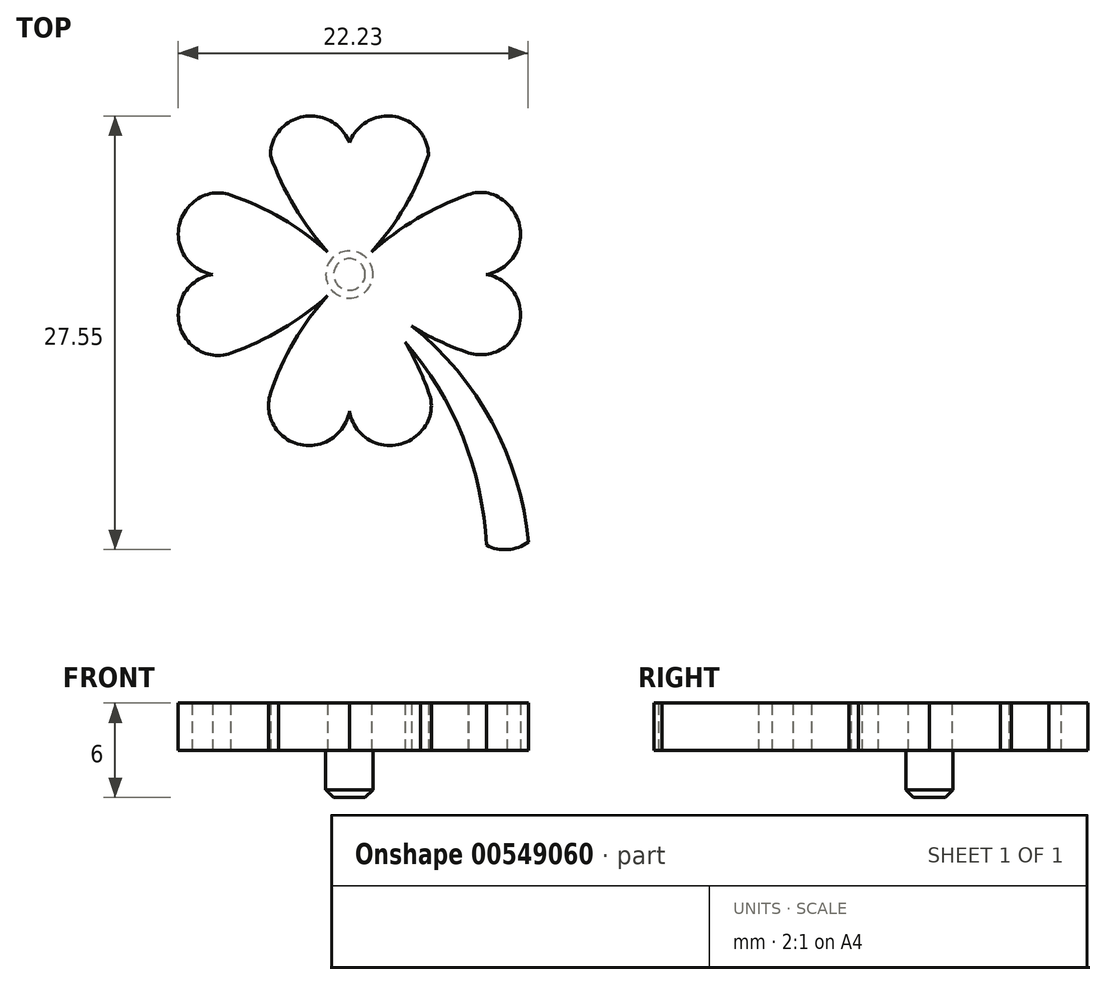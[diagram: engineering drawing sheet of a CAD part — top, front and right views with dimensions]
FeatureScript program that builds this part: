
annotation { "Feature Type Name" : "Feature", "Feature Type Description" : "" }
export const myFeature = defineFeature(function(context is Context, id is Id, definition is map)
    precondition{}
    {
        {
            var Q0;
            Q0=qCreatedBy(makeId("Top.planeOp"),FACE);
            var sketch = newSketch(context, id + "F0", { "sketchPlane" : qUnion([Q0])});
            skArc(sketch, "E0", {"start": v(-4.5, 9.05) * mm, "mid": v(-4.89, 8.35) * mm, "end": v(-5.02, 7.55) * mm});
            skArc(sketch, "E1", {"start": v(0, 8.36) * mm, "mid": v(-2.05, 10.04) * mm, "end": v(-4.5, 9.05) * mm});
            skLineSegment(sketch, "E2", {"start": v(0, 8.36) * mm, "end": v(0, 1.22) * mm, "construction": true});
            skLineSegment(sketch, "E3", {"start": v(0, 0) * mm, "end": v(0, 1.22) * mm, "construction": true});
            skArc(sketch, "E4.MirrorCS", {"start": v(4.5, 9.05) * mm, "mid": v(4.88, 8.36) * mm, "end": v(5.02, 7.6) * mm});
            skArc(sketch, "E5.MirrorCS", {"start": v(0, 8.36) * mm, "mid": v(2.05, 10.04) * mm, "end": v(4.5, 9.05) * mm});
            skArc(sketch, "E6.1.0", {"start": v(-10, 4.5) * mm, "mid": v(-8.85, 5.13) * mm, "end": v(-7.55, 5.05) * mm});
            skArc(sketch, "E6.1.1", {"start": v(-8.68, 0) * mm, "mid": v(-10.76, -1.84) * mm, "end": v(-10, -4.5) * mm});
            skLineSegment(sketch, "E6.1.2", {"start": v(-8.68, 0) * mm, "end": v(-1.22, 0) * mm, "construction": true});
            skArc(sketch, "E6.1.3", {"start": v(-10, -4.5) * mm, "mid": v(-8.82, -5.1) * mm, "end": v(-7.51, -5) * mm});
            skArc(sketch, "E6.1.4", {"start": v(-8.68, 0) * mm, "mid": v(-10.76, 1.84) * mm, "end": v(-10, 4.5) * mm});
            skArc(sketch, "E6.1.7", {"start": v(-8.68, 0) * mm, "mid": v(-10.76, -1.84) * mm, "end": v(-10, -4.5) * mm});
            skArc(sketch, "E6.1.8", {"start": v(-10, 4.5) * mm, "mid": v(-8.85, 5.13) * mm, "end": v(-7.55, 5.05) * mm});
            skArc(sketch, "E6.1.10", {"start": v(-8.68, 0) * mm, "mid": v(-10.76, 1.84) * mm, "end": v(-10, 4.5) * mm});
            skArc(sketch, "E6.1.11", {"start": v(-10, -4.5) * mm, "mid": v(-8.82, -5.1) * mm, "end": v(-7.51, -5) * mm});
            skArc(sketch, "E6.2.0", {"start": v(-4.5, -10) * mm, "mid": v(-5.09, -8.83) * mm, "end": v(-5, -7.53) * mm});
            skArc(sketch, "E6.2.1", {"start": v(0, -8.68) * mm, "mid": v(1.84, -10.76) * mm, "end": v(4.5, -10) * mm});
            skLineSegment(sketch, "E6.2.2", {"start": v(0, -8.68) * mm, "end": v(0, -1.22) * mm, "construction": true});
            skArc(sketch, "E6.2.3", {"start": v(4.5, -10) * mm, "mid": v(5.15, -8.82) * mm, "end": v(5.04, -7.49) * mm});
            skArc(sketch, "E6.2.4", {"start": v(0, -8.68) * mm, "mid": v(-1.84, -10.76) * mm, "end": v(-4.5, -10) * mm});
            skArc(sketch, "E6.2.7", {"start": v(0, -8.68) * mm, "mid": v(1.84, -10.76) * mm, "end": v(4.5, -10) * mm});
            skArc(sketch, "E6.2.8", {"start": v(-4.5, -10) * mm, "mid": v(-5.1, -8.83) * mm, "end": v(-5, -7.53) * mm});
            skArc(sketch, "E6.2.10", {"start": v(0, -8.68) * mm, "mid": v(-1.84, -10.76) * mm, "end": v(-4.5, -10) * mm});
            skArc(sketch, "E6.2.11", {"start": v(4.5, -10) * mm, "mid": v(5.15, -8.82) * mm, "end": v(5.04, -7.49) * mm});
            skArc(sketch, "E6.3.0", {"start": v(10, -4.5) * mm, "mid": v(8.84, -5.05) * mm, "end": v(7.57, -4.98) * mm});
            skArc(sketch, "E6.3.1", {"start": v(8.68, 0) * mm, "mid": v(10.76, 1.84) * mm, "end": v(10, 4.5) * mm});
            skLineSegment(sketch, "E6.3.2", {"start": v(8.68, 0) * mm, "end": v(1.22, 0) * mm, "construction": true});
            skArc(sketch, "E6.3.3", {"start": v(10, 4.5) * mm, "mid": v(8.85, 5.16) * mm, "end": v(7.53, 5.06) * mm});
            skArc(sketch, "E6.3.4", {"start": v(8.68, 0) * mm, "mid": v(10.76, -1.84) * mm, "end": v(10, -4.5) * mm});
            skArc(sketch, "E6.3.7", {"start": v(8.68, 0) * mm, "mid": v(10.76, 1.84) * mm, "end": v(10, 4.5) * mm});
            skArc(sketch, "E6.3.8", {"start": v(10, -4.5) * mm, "mid": v(8.84, -5.05) * mm, "end": v(7.57, -4.98) * mm});
            skArc(sketch, "E6.3.10", {"start": v(8.68, 0) * mm, "mid": v(10.76, -1.84) * mm, "end": v(10, -4.5) * mm});
            skArc(sketch, "E6.3.11", {"start": v(10, 4.5) * mm, "mid": v(8.85, 5.16) * mm, "end": v(7.53, 5.06) * mm});
            skPoint(sketch, "E6.center", {"position": v(0, 0) * mm});
            skArc(sketch, "E7", {"start": v(-1.38, -1.35) * mm, "mid": v(-3.5, -4.25) * mm, "end": v(-5, -7.53) * mm});
            skArc(sketch, "E8", {"start": v(-7.51, -5) * mm, "mid": v(-4.27, -3.47) * mm, "end": v(-1.38, -1.35) * mm});
            skPoint(sketch, "E9.orphan", {"position": v(-6.7, -4.5) * mm});
            skPoint(sketch, "E10.orphan", {"position": v(-6.69, -4.5) * mm});
            skPoint(sketch, "E11.orphan", {"position": v(-4.5, -6.69) * mm});
            skPoint(sketch, "E12.orphan", {"position": v(-4.52, -6.68) * mm});
            skArc(sketch, "E13.1.0", {"start": v(3.95, -3.28) * mm, "mid": v(5.71, -4.23) * mm, "end": v(7.57, -4.98) * mm});
            skArc(sketch, "E13.1.1", {"start": v(5.04, -7.49) * mm, "mid": v(4.37, -5.86) * mm, "end": v(3.54, -4.3) * mm});
            skArc(sketch, "E13.2.0", {"start": v(1.4, 1.42) * mm, "mid": v(3.53, 4.32) * mm, "end": v(5.02, 7.6) * mm});
            skArc(sketch, "E13.2.1", {"start": v(7.53, 5.06) * mm, "mid": v(4.29, 3.54) * mm, "end": v(1.4, 1.42) * mm});
            skArc(sketch, "E13.3.0", {"start": v(-1.38, 1.42) * mm, "mid": v(-4.28, 3.55) * mm, "end": v(-7.55, 5.05) * mm});
            skArc(sketch, "E13.3.1", {"start": v(-5.02, 7.55) * mm, "mid": v(-3.5, 4.31) * mm, "end": v(-1.38, 1.42) * mm});
            skPoint(sketch, "E13.center", {"position": v(0, 0.03) * mm});
            skPoint(sketch, "E14.orphan", {"position": v(-6.69, 4.5) * mm});
            skPoint(sketch, "E15.MirrorCS.end.orphan", {"position": v(0, 1.22) * mm});
            skPoint(sketch, "E16.orphan", {"position": v(4.5, 6.03) * mm});
            skPoint(sketch, "E17.orphan", {"position": v(-4.5, 6.03) * mm});
            skPoint(sketch, "E18.orphan", {"position": v(6.69, 4.5) * mm});
            skPoint(sketch, "E19.orphan", {"position": v(6.69, -4.5) * mm});
            skPoint(sketch, "E20.orphan", {"position": v(4.5, -6.69) * mm});
            skArc(sketch, "E21", {"start": v(8.7, -17.2) * mm, "mid": v(7.2, -10.31) * mm, "end": v(3.54, -4.3) * mm});
            skArc(sketch, "E22", {"start": v(11.36, -17) * mm, "mid": v(9.06, -9.38) * mm, "end": v(3.95, -3.28) * mm});
            skArc(sketch, "E23", {"start": v(8.7, -17.2) * mm, "mid": v(10.06, -17.48) * mm, "end": v(11.36, -17) * mm});
            skPoint(sketch, "E24.orphan", {"position": v(1.4, -1.35) * mm});
            skSolve(sketch);
        }
        {
            var Q0;
            Q0=makeQuery(id+"F0.imprint","IMPRINT",FACE,{"disambiguationData":[TD([[makeQuery(id+"F0.imprint","IMPRINT",EDGE,{"derivedFrom":sQuery(id+"F0.wireOp",EDGE,"E0")}),1.0]])]});
            extrude(context, id + "F1", {"entities" : qUnion([Q0]), "depth" : 3 * mm, "offsetDistance" : 25 * mm});
        }
        {
            var Q0;
            Q0=makeQuery(id+"F1.opExtrude","CAP_FACE",FACE,{"disambiguationData":[OSD([sQuery(id+"F0.wireOp",EDGE,"E0"),sQuery(id+"F0.wireOp",EDGE,"E1"),sQuery(id+"F0.wireOp",EDGE,"E5.MirrorCS"),sQuery(id+"F0.wireOp",EDGE,"E4.MirrorCS"),sQuery(id+"F0.wireOp",EDGE,"E6.1.7"),sQuery(id+"F0.wireOp",EDGE,"E6.1.8"),sQuery(id+"F0.wireOp",EDGE,"E6.1.10"),sQuery(id+"F0.wireOp",EDGE,"E6.1.11"),sQuery(id+"F0.wireOp",EDGE,"E6.2.0"),sQuery(id+"F0.wireOp",EDGE,"E6.2.7"),sQuery(id+"F0.wireOp",EDGE,"E6.2.10"),sQuery(id+"F0.wireOp",EDGE,"E6.2.11"),sQuery(id+"F0.wireOp",EDGE,"E6.3.7"),sQuery(id+"F0.wireOp",EDGE,"E6.3.8"),sQuery(id+"F0.wireOp",EDGE,"E6.3.10"),sQuery(id+"F0.wireOp",EDGE,"E6.3.11"),sQuery(id+"F0.wireOp",EDGE,"E7"),sQuery(id+"F0.wireOp",EDGE,"E8"),sQuery(id+"F0.wireOp",EDGE,"E13.1.0"),sQuery(id+"F0.wireOp",EDGE,"E13.1.1"),sQuery(id+"F0.wireOp",EDGE,"E13.2.0"),sQuery(id+"F0.wireOp",EDGE,"E13.2.1"),sQuery(id+"F0.wireOp",EDGE,"E13.3.0"),sQuery(id+"F0.wireOp",EDGE,"E13.3.1"),sQuery(id+"F0.wireOp",EDGE,"E21"),sQuery(id+"F0.wireOp",EDGE,"E22"),sQuery(id+"F0.wireOp",EDGE,"E23")])],"isStart":true});
            var sketch = newSketch(context, id + "F2", { "sketchPlane" : qUnion([Q0])});
            skCircle(sketch, "E25", {"center": v(0, 0) * mm, "radius": 1.5 * mm});
            skSolve(sketch);
        }
        {
            var Q0;
            Q0=makeQuery(id+"F2.imprint","IMPRINT",FACE,{"disambiguationData":[TD([[makeQuery(id+"F2.imprint","IMPRINT",EDGE,{"derivedFrom":sQuery(id+"F2.wireOp",EDGE,"E25")}),1.0]])]});
            extrude(context, id + "F3", {"entities" : qUnion([Q0]), "operationType" : NewBodyOperationType.ADD, "depth" : 3 * mm, "offsetDistance" : 25 * mm});
        }
        {
            var Q0;
            Q0=makeQuery(id+"F3.opExtrude","CAP_EDGE",EDGE,{"disambiguationData":[OSD([sQuery(id+"F2.wireOp",EDGE,"E25")])],"isStart":false});
            chamfer(context, id + "F4", {"entities" : qUnion([Q0]), "width" : 0.5 * mm, "tangentPropagation" : true});
        }
    });
